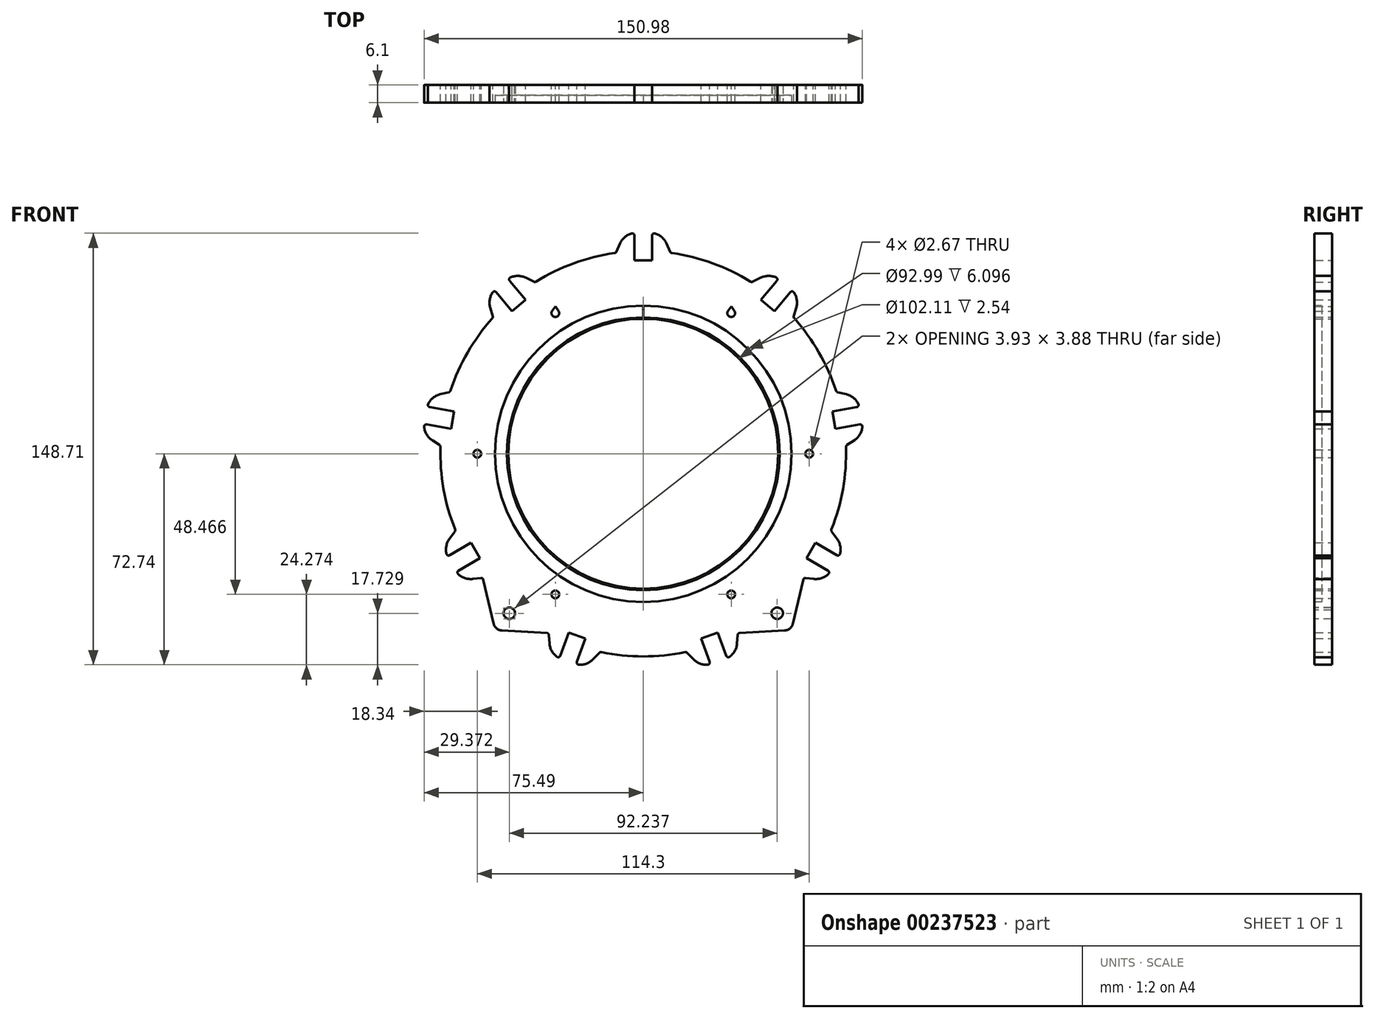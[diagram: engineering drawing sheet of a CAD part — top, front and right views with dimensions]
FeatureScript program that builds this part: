
annotation { "Feature Type Name" : "Feature", "Feature Type Description" : "" }
export const myFeature = defineFeature(function(context is Context, id is Id, definition is map)
    precondition{}
    {
        {
            var Q0;
            Q0=qCreatedBy(makeId("Front.planeOp"),FACE);
            var sketch = newSketch(context, id + "F0", { "sketchPlane" : qUnion([Q0])});
            skCircle(sketch, "E0", {"center": v(0, 0) * mm, "radius": 69.85 * mm});
            skCircle(sketch, "E1", {"center": v(0, 0) * mm, "radius": 46.5 * mm});
            skCircle(sketch, "E2", {"center": v(0, 0) * mm, "radius": 57.15 * mm, "construction": true});
            skPoint(sketch, "E3.center", {"position": v(0, -7.06) * mm});
            skLineSegment(sketch, "E4", {"start": v(-9.44, 69.2) * mm, "end": v(-8.02, 72.42) * mm});
            skLineSegment(sketch, "E5", {"start": v(-2.21, 76.2) * mm, "end": v(2.21, 76.2) * mm});
            skLineSegment(sketch, "E6", {"start": v(8.02, 72.42) * mm, "end": v(9.44, 69.2) * mm});
            skPoint(sketch, "E7", {"position": v(0, 76.2) * mm});
            skLineSegment(sketch, "E8", {"start": v(-3.05, 76.2) * mm, "end": v(-3.05, 66.67) * mm});
            skLineSegment(sketch, "E9", {"start": v(-3.05, 66.67) * mm, "end": v(3.05, 66.67) * mm});
            skLineSegment(sketch, "E10", {"start": v(3.05, 66.67) * mm, "end": v(3.05, 76.2) * mm});
            skPoint(sketch, "E11", {"position": v(0, 66.67) * mm});
            skPoint(sketch, "E12.visualSharp", {"position": v(-6.35, 76.2) * mm});
            skArc(sketch, "E12.filletArc", {"start": v(-2.21, 76.2) * mm, "mid": v(-5.68, 75.17) * mm, "end": v(-8.02, 72.42) * mm});
            skPoint(sketch, "E13.visualSharp", {"position": v(6.35, 76.2) * mm});
            skArc(sketch, "E13.filletArc", {"start": v(8.02, 72.42) * mm, "mid": v(5.68, 75.17) * mm, "end": v(2.21, 76.2) * mm});
            skCircle(sketch, "E14", {"center": v(0, 0) * mm, "radius": 66.72 * mm, "construction": true});
            skLineSegment(sketch, "E15.1.0", {"start": v(-51.72, 46.95) * mm, "end": v(-52.7, 50.32) * mm});
            skArc(sketch, "E15.1.1", {"start": v(-50.68, 56.95) * mm, "mid": v(-52.67, 53.93) * mm, "end": v(-52.7, 50.32) * mm});
            skLineSegment(sketch, "E15.1.2", {"start": v(-51.32, 56.41) * mm, "end": v(-45.2, 49.12) * mm});
            skLineSegment(sketch, "E15.1.3", {"start": v(-40.52, 53.04) * mm, "end": v(-46.65, 60.33) * mm});
            skArc(sketch, "E15.1.4", {"start": v(-40.4, 60.63) * mm, "mid": v(-43.97, 61.23) * mm, "end": v(-47.29, 59.8) * mm});
            skLineSegment(sketch, "E15.1.5", {"start": v(-40.4, 60.63) * mm, "end": v(-37.26, 59.08) * mm});
            skLineSegment(sketch, "E15.1.6", {"start": v(-45.2, 49.12) * mm, "end": v(-40.52, 53.04) * mm});
            skLineSegment(sketch, "E15.2.0", {"start": v(-69.8, 2.72) * mm, "end": v(-72.7, 4.68) * mm});
            skArc(sketch, "E15.2.1", {"start": v(-75.43, 11.05) * mm, "mid": v(-75.01, 7.46) * mm, "end": v(-72.7, 4.68) * mm});
            skLineSegment(sketch, "E15.2.2", {"start": v(-75.57, 10.23) * mm, "end": v(-66.2, 8.58) * mm});
            skLineSegment(sketch, "E15.2.3", {"start": v(-65.13, 14.58) * mm, "end": v(-74.51, 16.23) * mm});
            skArc(sketch, "E15.2.4", {"start": v(-69.92, 20.47) * mm, "mid": v(-73.04, 18.65) * mm, "end": v(-74.66, 15.41) * mm});
            skLineSegment(sketch, "E15.2.5", {"start": v(-69.92, 20.47) * mm, "end": v(-66.52, 21.31) * mm});
            skLineSegment(sketch, "E15.2.6", {"start": v(-66.2, 8.58) * mm, "end": v(-65.13, 14.58) * mm});
            skLineSegment(sketch, "E15.3.0", {"start": v(-55.22, -42.78) * mm, "end": v(-58.7, -43.15) * mm});
            skArc(sketch, "E15.3.1", {"start": v(-64.88, -40.02) * mm, "mid": v(-62.26, -42.5) * mm, "end": v(-58.7, -43.15) * mm});
            skLineSegment(sketch, "E15.3.2", {"start": v(-64.47, -40.74) * mm, "end": v(-56.22, -35.98) * mm});
            skLineSegment(sketch, "E15.3.3", {"start": v(-59.27, -30.7) * mm, "end": v(-67.52, -35.46) * mm});
            skArc(sketch, "E15.3.4", {"start": v(-66.72, -29.26) * mm, "mid": v(-67.94, -32.67) * mm, "end": v(-67.1, -36.18) * mm});
            skLineSegment(sketch, "E15.3.5", {"start": v(-66.72, -29.26) * mm, "end": v(-64.66, -26.43) * mm});
            skLineSegment(sketch, "E15.3.6", {"start": v(-56.22, -35.98) * mm, "end": v(-59.27, -30.7) * mm});
            skLineSegment(sketch, "E15.4.0", {"start": v(-14.8, -68.26) * mm, "end": v(-17.23, -70.8) * mm});
            skArc(sketch, "E15.4.1", {"start": v(-23.98, -72.36) * mm, "mid": v(-20.37, -72.58) * mm, "end": v(-17.23, -70.8) * mm});
            skLineSegment(sketch, "E15.4.2", {"start": v(-23.2, -72.65) * mm, "end": v(-19.94, -63.7) * mm});
            skLineSegment(sketch, "E15.4.3", {"start": v(-25.67, -61.61) * mm, "end": v(-28.93, -70.56) * mm});
            skArc(sketch, "E15.4.4", {"start": v(-32.3, -65.3) * mm, "mid": v(-31.05, -68.7) * mm, "end": v(-28.14, -70.85) * mm});
            skLineSegment(sketch, "E15.4.5", {"start": v(-32.3, -65.3) * mm, "end": v(-32.54, -61.8) * mm});
            skLineSegment(sketch, "E15.4.6", {"start": v(-19.94, -63.7) * mm, "end": v(-25.67, -61.61) * mm});
            skLineSegment(sketch, "E15.5.0", {"start": v(32.54, -61.8) * mm, "end": v(32.3, -65.3) * mm});
            skArc(sketch, "E15.5.1", {"start": v(28.14, -70.85) * mm, "mid": v(31.05, -68.7) * mm, "end": v(32.3, -65.3) * mm});
            skLineSegment(sketch, "E15.5.2", {"start": v(28.93, -70.56) * mm, "end": v(25.67, -61.61) * mm});
            skLineSegment(sketch, "E15.5.3", {"start": v(19.94, -63.7) * mm, "end": v(23.2, -72.65) * mm});
            skArc(sketch, "E15.5.4", {"start": v(17.23, -70.8) * mm, "mid": v(20.37, -72.58) * mm, "end": v(23.98, -72.36) * mm});
            skLineSegment(sketch, "E15.5.5", {"start": v(17.23, -70.8) * mm, "end": v(14.8, -68.26) * mm});
            skLineSegment(sketch, "E15.5.6", {"start": v(25.67, -61.61) * mm, "end": v(19.94, -63.7) * mm});
            skLineSegment(sketch, "E15.6.0", {"start": v(64.66, -26.43) * mm, "end": v(66.72, -29.26) * mm});
            skArc(sketch, "E15.6.1", {"start": v(67.1, -36.18) * mm, "mid": v(67.94, -32.67) * mm, "end": v(66.72, -29.26) * mm});
            skLineSegment(sketch, "E15.6.2", {"start": v(67.52, -35.46) * mm, "end": v(59.27, -30.7) * mm});
            skLineSegment(sketch, "E15.6.3", {"start": v(56.22, -35.98) * mm, "end": v(64.47, -40.74) * mm});
            skArc(sketch, "E15.6.4", {"start": v(58.7, -43.15) * mm, "mid": v(62.26, -42.5) * mm, "end": v(64.88, -40.02) * mm});
            skLineSegment(sketch, "E15.6.5", {"start": v(58.7, -43.15) * mm, "end": v(55.22, -42.78) * mm});
            skLineSegment(sketch, "E15.6.6", {"start": v(59.27, -30.7) * mm, "end": v(56.22, -35.98) * mm});
            skLineSegment(sketch, "E15.7.0", {"start": v(66.52, 21.31) * mm, "end": v(69.92, 20.47) * mm});
            skArc(sketch, "E15.7.1", {"start": v(74.66, 15.41) * mm, "mid": v(73.04, 18.65) * mm, "end": v(69.92, 20.47) * mm});
            skLineSegment(sketch, "E15.7.2", {"start": v(74.51, 16.23) * mm, "end": v(65.13, 14.58) * mm});
            skLineSegment(sketch, "E15.7.3", {"start": v(66.2, 8.58) * mm, "end": v(75.57, 10.23) * mm});
            skArc(sketch, "E15.7.4", {"start": v(72.7, 4.68) * mm, "mid": v(75.01, 7.46) * mm, "end": v(75.43, 11.05) * mm});
            skLineSegment(sketch, "E15.7.5", {"start": v(72.7, 4.68) * mm, "end": v(69.8, 2.72) * mm});
            skLineSegment(sketch, "E15.7.6", {"start": v(65.13, 14.58) * mm, "end": v(66.2, 8.58) * mm});
            skLineSegment(sketch, "E15.8.0", {"start": v(37.26, 59.08) * mm, "end": v(40.4, 60.63) * mm});
            skArc(sketch, "E15.8.1", {"start": v(47.29, 59.8) * mm, "mid": v(43.97, 61.23) * mm, "end": v(40.4, 60.63) * mm});
            skLineSegment(sketch, "E15.8.2", {"start": v(46.65, 60.33) * mm, "end": v(40.52, 53.04) * mm});
            skLineSegment(sketch, "E15.8.3", {"start": v(45.2, 49.12) * mm, "end": v(51.32, 56.41) * mm});
            skArc(sketch, "E15.8.4", {"start": v(52.7, 50.32) * mm, "mid": v(52.67, 53.93) * mm, "end": v(50.68, 56.95) * mm});
            skLineSegment(sketch, "E15.8.5", {"start": v(52.7, 50.32) * mm, "end": v(51.72, 46.95) * mm});
            skLineSegment(sketch, "E15.8.6", {"start": v(40.52, 53.04) * mm, "end": v(45.2, 49.12) * mm});
            skCircle(sketch, "E16", {"center": v(57.15, 0) * mm, "radius": 1.33 * mm});
            skCircle(sketch, "E17", {"center": v(30.28, 48.47) * mm, "radius": 1.33 * mm});
            skCircle(sketch, "E18", {"center": v(30.28, -48.47) * mm, "radius": 1.33 * mm});
            skLineSegment(sketch, "E19", {"start": v(0, 0) * mm, "end": v(30.28, -48.47) * mm, "construction": true});
            skLineSegment(sketch, "E20", {"start": v(30.28, 48.47) * mm, "end": v(0, 0) * mm, "construction": true});
            skCircle(sketch, "E21.MirrorC", {"center": v(-30.28, -48.47) * mm, "radius": 1.33 * mm});
            skCircle(sketch, "E22.MirrorC", {"center": v(-57.15, 0) * mm, "radius": 1.33 * mm});
            skCircle(sketch, "E23.MirrorC", {"center": v(-30.28, 48.47) * mm, "radius": 1.33 * mm});
            skLineSegment(sketch, "E24", {"start": v(31.38, 49.23) * mm, "end": v(30.28, 50.78) * mm});
            skLineSegment(sketch, "E25", {"start": v(30.28, 50.78) * mm, "end": v(29.2, 49.23) * mm});
            skLineSegment(sketch, "E26", {"start": v(-31.38, 49.23) * mm, "end": v(-30.28, 50.78) * mm});
            skLineSegment(sketch, "E27", {"start": v(-30.28, 50.78) * mm, "end": v(-29.2, 49.23) * mm});
            skArc(sketch, "E28", {"start": v(-2.21, 76.2) * mm, "mid": v(-8.62, 74.13) * mm, "end": v(-12.61, 68.7) * mm});
            skArc(sketch, "E29", {"start": v(12.61, 68.7) * mm, "mid": v(9.12, 74.1) * mm, "end": v(3.05, 76.2) * mm});
            skSolve(sketch);
        }
        {
            var Q0;
            Q0=makeQuery(id+"F0.imprint","IMPRINT",FACE,{"disambiguationData":[TD([[makeQuery(id+"F0.imprint","IMPRINT",EDGE,{"derivedFrom":sQuery(id+"F0.wireOp",EDGE,"E1")}),-1.0]])]});
            var Q1;
            {var subQ0=sQuery(id+"F0.wireOp",EDGE,"E15.1.5");Q1=makeQuery(id+"F0.imprint","IMPRINT",FACE,{"disambiguationData":[TD([[makeQuery(id+"F0.imprint","IMPRINT",EDGE,{"derivedFrom":subQ0}),-1.0]])]});}
            var Q2;
            {var subQ0=sQuery(id+"F0.wireOp",EDGE,"E15.1.0");Q2=makeQuery(id+"F0.imprint","IMPRINT",FACE,{"disambiguationData":[TD([[makeQuery(id+"F0.imprint","IMPRINT",EDGE,{"derivedFrom":subQ0}),-1.0]])]});}
            var Q3;
            {var subQ0=sQuery(id+"F0.wireOp",EDGE,"E4");Q3=makeQuery(id+"F0.imprint","IMPRINT",FACE,{"disambiguationData":[TD([[makeQuery(id+"F0.imprint","IMPRINT",EDGE,{"derivedFrom":subQ0}),-1.0]])]});}
            var Q4;
            {var subQ0=sQuery(id+"F0.wireOp",EDGE,"E6");Q4=makeQuery(id+"F0.imprint","IMPRINT",FACE,{"disambiguationData":[TD([[makeQuery(id+"F0.imprint","IMPRINT",EDGE,{"derivedFrom":subQ0}),-1.0]])]});}
            var Q5;
            {var subQ0=sQuery(id+"F0.wireOp",EDGE,"E15.8.0");Q5=makeQuery(id+"F0.imprint","IMPRINT",FACE,{"disambiguationData":[TD([[makeQuery(id+"F0.imprint","IMPRINT",EDGE,{"derivedFrom":subQ0}),-1.0]])]});}
            var Q6;
            {var subQ0=sQuery(id+"F0.wireOp",EDGE,"E15.8.5");Q6=makeQuery(id+"F0.imprint","IMPRINT",FACE,{"disambiguationData":[TD([[makeQuery(id+"F0.imprint","IMPRINT",EDGE,{"derivedFrom":subQ0}),-1.0]])]});}
            var Q7;
            {var subQ0=sQuery(id+"F0.wireOp",EDGE,"E15.7.0");Q7=makeQuery(id+"F0.imprint","IMPRINT",FACE,{"disambiguationData":[TD([[makeQuery(id+"F0.imprint","IMPRINT",EDGE,{"derivedFrom":subQ0}),-1.0]])]});}
            var Q8;
            {var subQ0=sQuery(id+"F0.wireOp",EDGE,"E15.7.5");Q8=makeQuery(id+"F0.imprint","IMPRINT",FACE,{"disambiguationData":[TD([[makeQuery(id+"F0.imprint","IMPRINT",EDGE,{"derivedFrom":subQ0}),-1.0]])]});}
            var Q9;
            {var subQ0=sQuery(id+"F0.wireOp",EDGE,"E15.6.0");Q9=makeQuery(id+"F0.imprint","IMPRINT",FACE,{"disambiguationData":[TD([[makeQuery(id+"F0.imprint","IMPRINT",EDGE,{"derivedFrom":subQ0}),-1.0]])]});}
            var Q10;
            {var subQ0=sQuery(id+"F0.wireOp",EDGE,"E15.6.5");Q10=makeQuery(id+"F0.imprint","IMPRINT",FACE,{"disambiguationData":[TD([[makeQuery(id+"F0.imprint","IMPRINT",EDGE,{"derivedFrom":subQ0}),-1.0]])]});}
            var Q11;
            {var subQ0=sQuery(id+"F0.wireOp",EDGE,"E15.5.5");Q11=makeQuery(id+"F0.imprint","IMPRINT",FACE,{"disambiguationData":[TD([[makeQuery(id+"F0.imprint","IMPRINT",EDGE,{"derivedFrom":subQ0}),-1.0]])]});}
            var Q12;
            {var subQ0=sQuery(id+"F0.wireOp",EDGE,"E15.5.0");Q12=makeQuery(id+"F0.imprint","IMPRINT",FACE,{"disambiguationData":[TD([[makeQuery(id+"F0.imprint","IMPRINT",EDGE,{"derivedFrom":subQ0}),-1.0]])]});}
            var Q13;
            {var subQ0=sQuery(id+"F0.wireOp",EDGE,"E15.4.5");Q13=makeQuery(id+"F0.imprint","IMPRINT",FACE,{"disambiguationData":[TD([[makeQuery(id+"F0.imprint","IMPRINT",EDGE,{"derivedFrom":subQ0}),-1.0]])]});}
            var Q14;
            {var subQ0=sQuery(id+"F0.wireOp",EDGE,"E15.4.0");Q14=makeQuery(id+"F0.imprint","IMPRINT",FACE,{"disambiguationData":[TD([[makeQuery(id+"F0.imprint","IMPRINT",EDGE,{"derivedFrom":subQ0}),-1.0]])]});}
            var Q15;
            {var subQ0=sQuery(id+"F0.wireOp",EDGE,"E15.3.0");Q15=makeQuery(id+"F0.imprint","IMPRINT",FACE,{"disambiguationData":[TD([[makeQuery(id+"F0.imprint","IMPRINT",EDGE,{"derivedFrom":subQ0}),-1.0]])]});}
            var Q16;
            {var subQ0=sQuery(id+"F0.wireOp",EDGE,"E15.3.5");Q16=makeQuery(id+"F0.imprint","IMPRINT",FACE,{"disambiguationData":[TD([[makeQuery(id+"F0.imprint","IMPRINT",EDGE,{"derivedFrom":subQ0}),-1.0]])]});}
            var Q17;
            {var subQ0=sQuery(id+"F0.wireOp",EDGE,"E15.2.0");Q17=makeQuery(id+"F0.imprint","IMPRINT",FACE,{"disambiguationData":[TD([[makeQuery(id+"F0.imprint","IMPRINT",EDGE,{"derivedFrom":subQ0}),-1.0]])]});}
            var Q18;
            {var subQ0=sQuery(id+"F0.wireOp",EDGE,"E15.2.5");Q18=makeQuery(id+"F0.imprint","IMPRINT",FACE,{"disambiguationData":[TD([[makeQuery(id+"F0.imprint","IMPRINT",EDGE,{"derivedFrom":subQ0}),-1.0]])]});}
            extrude(context, id + "F1", {"entities" : qUnion([Q0, Q1, Q2, Q3, Q4, Q5, Q6, Q7, Q8, Q9, Q10, Q11, Q12, Q13, Q14, Q15, Q16, Q17, Q18]), "offsetDistance" : 25.4 * mm, "depth" : 6.1 * mm});
        }
        {
            var Q0;
            Q0=makeQuery(id+"F1.opExtrude","CAP_FACE",FACE,{"disambiguationData":[OSD([sQuery(id+"F0.wireOp",EDGE,"E0"),sQuery(id+"F0.wireOp",EDGE,"E1"),sQuery(id+"F0.wireOp",EDGE,"s7rXqqL2-3z2l-88EV-UIsY-hwb08Po9ZJjJ"),sQuery(id+"F0.wireOp",EDGE,"E3.1.0"),sQuery(id+"F0.wireOp",EDGE,"E3.2.0"),sQuery(id+"F0.wireOp",EDGE,"E3.3.0"),sQuery(id+"F0.wireOp",EDGE,"E4"),sQuery(id+"F0.wireOp",EDGE,"E6"),sQuery(id+"F0.wireOp",EDGE,"E8"),sQuery(id+"F0.wireOp",EDGE,"E9"),sQuery(id+"F0.wireOp",EDGE,"E10"),sQuery(id+"F0.wireOp",EDGE,"E12.filletArc"),sQuery(id+"F0.wireOp",EDGE,"E13.filletArc"),sQuery(id+"F0.wireOp",EDGE,"e3144966-756d-47fd-8283-5f46bd2110e0.1.0"),sQuery(id+"F0.wireOp",EDGE,"e3144966-756d-47fd-8283-5f46bd2110e0.1.1"),sQuery(id+"F0.wireOp",EDGE,"e3144966-756d-47fd-8283-5f46bd2110e0.1.2"),sQuery(id+"F0.wireOp",EDGE,"e3144966-756d-47fd-8283-5f46bd2110e0.1.3"),sQuery(id+"F0.wireOp",EDGE,"e3144966-756d-47fd-8283-5f46bd2110e0.1.4"),sQuery(id+"F0.wireOp",EDGE,"e3144966-756d-47fd-8283-5f46bd2110e0.1.6"),sQuery(id+"F0.wireOp",EDGE,"e3144966-756d-47fd-8283-5f46bd2110e0.1.7"),sQuery(id+"F0.wireOp",EDGE,"e3144966-756d-47fd-8283-5f46bd2110e0.2.0"),sQuery(id+"F0.wireOp",EDGE,"e3144966-756d-47fd-8283-5f46bd2110e0.2.1"),sQuery(id+"F0.wireOp",EDGE,"e3144966-756d-47fd-8283-5f46bd2110e0.2.2"),sQuery(id+"F0.wireOp",EDGE,"e3144966-756d-47fd-8283-5f46bd2110e0.2.3"),sQuery(id+"F0.wireOp",EDGE,"e3144966-756d-47fd-8283-5f46bd2110e0.2.4"),sQuery(id+"F0.wireOp",EDGE,"e3144966-756d-47fd-8283-5f46bd2110e0.2.6"),sQuery(id+"F0.wireOp",EDGE,"e3144966-756d-47fd-8283-5f46bd2110e0.2.7"),sQuery(id+"F0.wireOp",EDGE,"e3144966-756d-47fd-8283-5f46bd2110e0.3.0"),sQuery(id+"F0.wireOp",EDGE,"e3144966-756d-47fd-8283-5f46bd2110e0.3.1"),sQuery(id+"F0.wireOp",EDGE,"e3144966-756d-47fd-8283-5f46bd2110e0.3.2"),sQuery(id+"F0.wireOp",EDGE,"e3144966-756d-47fd-8283-5f46bd2110e0.3.3"),sQuery(id+"F0.wireOp",EDGE,"e3144966-756d-47fd-8283-5f46bd2110e0.3.4"),sQuery(id+"F0.wireOp",EDGE,"e3144966-756d-47fd-8283-5f46bd2110e0.3.6"),sQuery(id+"F0.wireOp",EDGE,"e3144966-756d-47fd-8283-5f46bd2110e0.3.7"),sQuery(id+"F0.wireOp",EDGE,"e3144966-756d-47fd-8283-5f46bd2110e0.4.0"),sQuery(id+"F0.wireOp",EDGE,"e3144966-756d-47fd-8283-5f46bd2110e0.4.1"),sQuery(id+"F0.wireOp",EDGE,"e3144966-756d-47fd-8283-5f46bd2110e0.4.2"),sQuery(id+"F0.wireOp",EDGE,"e3144966-756d-47fd-8283-5f46bd2110e0.4.3"),sQuery(id+"F0.wireOp",EDGE,"e3144966-756d-47fd-8283-5f46bd2110e0.4.4"),sQuery(id+"F0.wireOp",EDGE,"e3144966-756d-47fd-8283-5f46bd2110e0.4.6"),sQuery(id+"F0.wireOp",EDGE,"e3144966-756d-47fd-8283-5f46bd2110e0.4.7"),sQuery(id+"F0.wireOp",EDGE,"e3144966-756d-47fd-8283-5f46bd2110e0.5.0"),sQuery(id+"F0.wireOp",EDGE,"e3144966-756d-47fd-8283-5f46bd2110e0.5.1"),sQuery(id+"F0.wireOp",EDGE,"e3144966-756d-47fd-8283-5f46bd2110e0.5.2"),sQuery(id+"F0.wireOp",EDGE,"e3144966-756d-47fd-8283-5f46bd2110e0.5.3"),sQuery(id+"F0.wireOp",EDGE,"e3144966-756d-47fd-8283-5f46bd2110e0.5.4"),sQuery(id+"F0.wireOp",EDGE,"e3144966-756d-47fd-8283-5f46bd2110e0.5.6"),sQuery(id+"F0.wireOp",EDGE,"e3144966-756d-47fd-8283-5f46bd2110e0.5.7"),sQuery(id+"F0.wireOp",EDGE,"e3144966-756d-47fd-8283-5f46bd2110e0.6.0"),sQuery(id+"F0.wireOp",EDGE,"e3144966-756d-47fd-8283-5f46bd2110e0.6.1"),sQuery(id+"F0.wireOp",EDGE,"e3144966-756d-47fd-8283-5f46bd2110e0.6.2"),sQuery(id+"F0.wireOp",EDGE,"e3144966-756d-47fd-8283-5f46bd2110e0.6.3"),sQuery(id+"F0.wireOp",EDGE,"e3144966-756d-47fd-8283-5f46bd2110e0.6.4"),sQuery(id+"F0.wireOp",EDGE,"e3144966-756d-47fd-8283-5f46bd2110e0.6.6"),sQuery(id+"F0.wireOp",EDGE,"e3144966-756d-47fd-8283-5f46bd2110e0.6.7"),sQuery(id+"F0.wireOp",EDGE,"e3144966-756d-47fd-8283-5f46bd2110e0.7.0"),sQuery(id+"F0.wireOp",EDGE,"e3144966-756d-47fd-8283-5f46bd2110e0.7.1"),sQuery(id+"F0.wireOp",EDGE,"e3144966-756d-47fd-8283-5f46bd2110e0.7.2"),sQuery(id+"F0.wireOp",EDGE,"e3144966-756d-47fd-8283-5f46bd2110e0.7.3"),sQuery(id+"F0.wireOp",EDGE,"e3144966-756d-47fd-8283-5f46bd2110e0.7.4"),sQuery(id+"F0.wireOp",EDGE,"e3144966-756d-47fd-8283-5f46bd2110e0.7.6"),sQuery(id+"F0.wireOp",EDGE,"e3144966-756d-47fd-8283-5f46bd2110e0.7.7"),sQuery(id+"F0.wireOp",EDGE,"e3144966-756d-47fd-8283-5f46bd2110e0.8.0"),sQuery(id+"F0.wireOp",EDGE,"e3144966-756d-47fd-8283-5f46bd2110e0.8.1"),sQuery(id+"F0.wireOp",EDGE,"e3144966-756d-47fd-8283-5f46bd2110e0.8.2"),sQuery(id+"F0.wireOp",EDGE,"e3144966-756d-47fd-8283-5f46bd2110e0.8.3"),sQuery(id+"F0.wireOp",EDGE,"e3144966-756d-47fd-8283-5f46bd2110e0.8.4"),sQuery(id+"F0.wireOp",EDGE,"e3144966-756d-47fd-8283-5f46bd2110e0.8.6"),sQuery(id+"F0.wireOp",EDGE,"e3144966-756d-47fd-8283-5f46bd2110e0.8.7")])],"isStart":false});
            var sketch = newSketch(context, id + "F2", { "sketchPlane" : qUnion([Q0])});
            skCircle(sketch, "E30", {"center": v(0, 0) * mm, "radius": 47 * mm});
            skCircle(sketch, "E31", {"center": v(0, 0) * mm, "radius": 51.05 * mm});
            skSolve(sketch);
        }
        {
            var Q0;
            Q0=makeQuery(id+"F2.imprint","IMPRINT",FACE,{"disambiguationData":[TD([[makeQuery(id+"F2.imprint","IMPRINT",EDGE,{"derivedFrom":sQuery(id+"F2.wireOp",EDGE,"E31")}),1.0]])]});
            extrude(context, id + "F3", {"entities" : qUnion([Q0]), "operationType" : NewBodyOperationType.REMOVE, "oppositeDirection" : true, "depth" : 2.54 * mm});
        }
        {
            var Q0;
            {var subQ0=sQuery(id+"F0.wireOp",EDGE,"E15.5.2");var subQ1=sQuery(id+"F0.wireOp",EDGE,"E15.5.0");var subQ2=sQuery(id+"F0.wireOp",EDGE,"E15.5.5");var subQ3=sQuery(id+"F0.wireOp",EDGE,"E15.4.5");var subQ4=sQuery(id+"F0.wireOp",EDGE,"E15.4.6");var subQ5=sQuery(id+"F0.wireOp",EDGE,"E15.4.4");var subQ6=sQuery(id+"F0.wireOp",EDGE,"E15.5.3");var subQ7=sQuery(id+"F0.wireOp",EDGE,"E15.4.2");var subQ8=sQuery(id+"F0.wireOp",EDGE,"E15.4.0");var subQ9=sQuery(id+"F0.wireOp",EDGE,"E15.3.5");var subQ10=sQuery(id+"F0.wireOp",EDGE,"E15.3.3");var subQ11=sQuery(id+"F0.wireOp",EDGE,"E15.2.5");var subQ12=sQuery(id+"F0.wireOp",EDGE,"E15.3.1");var subQ13=sQuery(id+"F0.wireOp",EDGE,"E29");var subQ14=sQuery(id+"F0.wireOp",EDGE,"E15.5.4");var subQ15=sQuery(id+"F0.wireOp",EDGE,"E15.4.3");var subQ16=sQuery(id+"F0.wireOp",EDGE,"E15.4.1");var subQ17=sQuery(id+"F0.wireOp",EDGE,"E15.3.0");var subQ18=sQuery(id+"F0.wireOp",EDGE,"E28");var subQ19=sQuery(id+"F0.wireOp",EDGE,"E15.2.6");var subQ20=sQuery(id+"F0.wireOp",EDGE,"E27");var subQ21=sQuery(id+"F0.wireOp",EDGE,"E15.2.4");var subQ22=sQuery(id+"F0.wireOp",EDGE,"E25");var subQ23=sQuery(id+"F0.wireOp",EDGE,"E15.3.6");var subQ24=sQuery(id+"F0.wireOp",EDGE,"E15.3.4");var subQ25=sQuery(id+"F0.wireOp",EDGE,"E15.2.3");var subQ26=sQuery(id+"F0.wireOp",EDGE,"E0");var subQ27=sQuery(id+"F0.wireOp",EDGE,"E15.6.5");var subQ28=sQuery(id+"F0.wireOp",EDGE,"E15.7.4");var subQ29=sQuery(id+"F0.wireOp",EDGE,"E15.1.1");var subQ30=sQuery(id+"F0.wireOp",EDGE,"E17");var subQ31=sQuery(id+"F0.wireOp",EDGE,"E15.2.0");var subQ32=sQuery(id+"F0.wireOp",EDGE,"E15.2.2");var subQ33=sQuery(id+"F0.wireOp",EDGE,"E23.MirrorC");var subQ34=sQuery(id+"F0.wireOp",EDGE,"E15.7.0");var subQ35=sQuery(id+"F0.wireOp",EDGE,"E15.8.5");var subQ36=sQuery(id+"F0.wireOp",EDGE,"E15.8.0");var subQ37=sQuery(id+"F0.wireOp",EDGE,"E15.8.4");var subQ38=sQuery(id+"F0.wireOp",EDGE,"E15.1.5");var subQ39=sQuery(id+"F0.wireOp",EDGE,"E15.5.1");var subQ40=sQuery(id+"F0.wireOp",EDGE,"E15.1.0");var subQ41=sQuery(id+"F0.wireOp",EDGE,"E9");var subQ42=sQuery(id+"F0.wireOp",EDGE,"E15.8.1");var subQ43=sQuery(id+"F0.wireOp",EDGE,"E15.1.2");var subQ44=sQuery(id+"F0.wireOp",EDGE,"E15.7.3");var subQ45=sQuery(id+"F0.wireOp",EDGE,"E15.1.4");var subQ46=sQuery(id+"F0.wireOp",EDGE,"E8");var subQ47=sQuery(id+"F0.wireOp",EDGE,"E15.3.2");var subQ48=sQuery(id+"F0.wireOp",EDGE,"E15.2.1");var subQ49=sQuery(id+"F0.wireOp",EDGE,"E15.1.6");var subQ50=sQuery(id+"F0.wireOp",EDGE,"E15.8.3");var subQ51=sQuery(id+"F0.wireOp",EDGE,"E10");var subQ52=sQuery(id+"F0.wireOp",EDGE,"E15.8.2");var subQ53=sQuery(id+"F0.wireOp",EDGE,"E15.6.0");var subQ54=sQuery(id+"F0.wireOp",EDGE,"E15.7.5");var subQ55=sQuery(id+"F0.wireOp",EDGE,"E15.1.3");var subQ56=sQuery(id+"F0.wireOp",EDGE,"E15.5.6");var subQ57=sQuery(id+"F0.wireOp",EDGE,"E26");var subQ58=sQuery(id+"F0.wireOp",EDGE,"E15.6.1");var subQ59=sQuery(id+"F0.wireOp",EDGE,"E15.6.2");var subQ60=sQuery(id+"F0.wireOp",EDGE,"E15.6.3");var subQ61=sQuery(id+"F0.wireOp",EDGE,"E15.6.4");var subQ62=sQuery(id+"F0.wireOp",EDGE,"E24");var subQ63=sQuery(id+"F0.wireOp",EDGE,"E15.6.6");var subQ64=sQuery(id+"F0.wireOp",EDGE,"E15.7.1");var subQ65=sQuery(id+"F0.wireOp",EDGE,"E15.7.2");var subQ66=sQuery(id+"F0.wireOp",EDGE,"E15.7.6");var subQ67=sQuery(id+"F0.wireOp",EDGE,"E15.8.6");var subQ68=sQuery(id+"F0.wireOp",EDGE,"E16");var subQ69=sQuery(id+"F0.wireOp",EDGE,"E18");var subQ70=sQuery(id+"F0.wireOp",EDGE,"E21.MirrorC");var subQ71=sQuery(id+"F0.wireOp",EDGE,"E22.MirrorC");Q0=makeQuery(id+"F3.boolean.opBoolean","SPLIT",FACE,{"disambiguationData":[TD([makeQuery(id+"F1.opExtrude","SWEPT_FACE",FACE,{"disambiguationData":[OSD([subQ46])]})])],"derivedFrom":makeQuery(id+"F1.opExtrude","CAP_FACE",FACE,{"disambiguationData":[OSD([subQ26,sQuery(id+"F0.wireOp",EDGE,"E1"),subQ46,subQ41,subQ51,subQ40,subQ29,subQ43,subQ55,subQ45,subQ38,subQ49,subQ31,subQ48,subQ32,subQ25,subQ21,subQ11,subQ19,subQ17,subQ12,subQ47,subQ10,subQ24,subQ9,subQ23,subQ8,subQ16,subQ7,subQ15,subQ5,subQ3,subQ4,subQ1,subQ39,subQ0,subQ6,subQ14,subQ2,subQ56,subQ53,subQ58,subQ59,subQ60,subQ61,subQ27,subQ63,subQ34,subQ64,subQ65,subQ44,subQ28,subQ54,subQ66,subQ36,subQ42,subQ52,subQ50,subQ37,subQ35,subQ67,subQ68,subQ30,subQ69,subQ70,subQ71,subQ33,subQ62,subQ22,subQ57,subQ20,subQ18,subQ13])],"isStart":false})});}
            var sketch = newSketch(context, id + "F4", { "sketchPlane" : qUnion([Q0])});
            skLineSegment(sketch, "E32", {"start": v(-0.03, 51.05) * mm, "end": v(-0.03, 46.99) * mm});
            skLineSegment(sketch, "E33", {"start": v(0.03, 46.99) * mm, "end": v(0.03, 51.05) * mm});
            skArc(sketch, "E34", {"start": v(0.03, 46.99) * mm, "mid": v(0, 46.99) * mm, "end": v(-0.03, 46.99) * mm});
            skArc(sketch, "E35", {"start": v(0.03, 51.05) * mm, "mid": v(0, 51.05) * mm, "end": v(-0.03, 51.05) * mm});
            skPoint(sketch, "E36.positionSnap0", {"position": v(0, 47) * mm});
            skSolve(sketch);
        }
        {
            var Q0;
            Q0=qSketchRegion(id+"F4",true);
            var Q1;
            Q1=makeQuery(id+"F3.boolean.opBoolean","COPY",FACE,{"derivedFrom":makeQuery(id+"F3.opExtrude","CAP_FACE",FACE,{"disambiguationData":[OSD([sQuery(id+"F2.wireOp",EDGE,"E30"),sQuery(id+"F2.wireOp",EDGE,"E31")])],"isStart":false})});
            extrude(context, id + "F5", {"entities" : qUnion([Q0]), "operationType" : NewBodyOperationType.ADD, "endBound" : BoundingType.UP_TO_SURFACE, "oppositeDirection" : true, "endBoundEntityFace" : qUnion([Q1]), "depth" : 25.4 * mm});
        }
        {
            var Q0;
            {var subQ0=sQuery(id+"F4.wireOp",EDGE,"E35");var subQ1=sQuery(id+"F4.wireOp",EDGE,"E34");var subQ2=sQuery(id+"F4.wireOp",EDGE,"E33");var subQ3=sQuery(id+"F4.wireOp",EDGE,"E32");var subQ4=sQuery(id+"F0.wireOp",EDGE,"E1");var subQ5=sQuery(id+"F0.wireOp",EDGE,"E27");var subQ6=sQuery(id+"F0.wireOp",EDGE,"E26");var subQ7=sQuery(id+"F0.wireOp",EDGE,"E25");var subQ8=sQuery(id+"F0.wireOp",EDGE,"E24");var subQ9=sQuery(id+"F0.wireOp",EDGE,"E23.MirrorC");var subQ10=sQuery(id+"F0.wireOp",EDGE,"E22.MirrorC");var subQ11=sQuery(id+"F0.wireOp",EDGE,"E21.MirrorC");var subQ12=sQuery(id+"F0.wireOp",EDGE,"E18");var subQ13=sQuery(id+"F0.wireOp",EDGE,"E17");var subQ14=sQuery(id+"F0.wireOp",EDGE,"E16");var subQ15=sQuery(id+"F0.wireOp",EDGE,"E15.8.6");var subQ16=sQuery(id+"F0.wireOp",EDGE,"E15.8.5");var subQ17=sQuery(id+"F0.wireOp",EDGE,"E15.8.4");var subQ18=sQuery(id+"F0.wireOp",EDGE,"E15.8.3");var subQ19=sQuery(id+"F0.wireOp",EDGE,"E15.8.2");var subQ20=sQuery(id+"F0.wireOp",EDGE,"E15.8.1");var subQ21=sQuery(id+"F0.wireOp",EDGE,"E15.8.0");var subQ22=sQuery(id+"F0.wireOp",EDGE,"E15.7.6");var subQ23=sQuery(id+"F0.wireOp",EDGE,"E15.7.5");var subQ24=sQuery(id+"F0.wireOp",EDGE,"E15.7.4");var subQ25=sQuery(id+"F0.wireOp",EDGE,"E15.7.3");var subQ26=sQuery(id+"F0.wireOp",EDGE,"E15.7.2");var subQ27=sQuery(id+"F0.wireOp",EDGE,"E15.7.1");var subQ28=sQuery(id+"F0.wireOp",EDGE,"E15.7.0");var subQ29=sQuery(id+"F0.wireOp",EDGE,"E15.6.6");var subQ30=sQuery(id+"F0.wireOp",EDGE,"E15.6.5");var subQ31=sQuery(id+"F0.wireOp",EDGE,"E15.6.4");var subQ32=sQuery(id+"F0.wireOp",EDGE,"E15.6.3");var subQ33=sQuery(id+"F0.wireOp",EDGE,"E15.6.2");var subQ34=sQuery(id+"F0.wireOp",EDGE,"E15.6.1");var subQ35=sQuery(id+"F0.wireOp",EDGE,"E15.6.0");var subQ36=sQuery(id+"F0.wireOp",EDGE,"E15.5.6");var subQ37=sQuery(id+"F0.wireOp",EDGE,"E15.5.5");var subQ38=sQuery(id+"F0.wireOp",EDGE,"E15.5.4");var subQ39=sQuery(id+"F0.wireOp",EDGE,"E15.5.3");var subQ40=sQuery(id+"F0.wireOp",EDGE,"E15.5.2");var subQ41=sQuery(id+"F0.wireOp",EDGE,"E15.5.1");var subQ42=sQuery(id+"F0.wireOp",EDGE,"E15.5.0");var subQ43=sQuery(id+"F0.wireOp",EDGE,"E15.4.6");var subQ44=sQuery(id+"F0.wireOp",EDGE,"E15.4.5");var subQ45=sQuery(id+"F0.wireOp",EDGE,"E15.4.4");var subQ46=sQuery(id+"F0.wireOp",EDGE,"E15.4.3");var subQ47=sQuery(id+"F0.wireOp",EDGE,"E15.4.2");var subQ48=sQuery(id+"F0.wireOp",EDGE,"E15.4.1");var subQ49=sQuery(id+"F0.wireOp",EDGE,"E15.4.0");var subQ50=sQuery(id+"F0.wireOp",EDGE,"E15.3.6");var subQ51=sQuery(id+"F0.wireOp",EDGE,"E15.3.5");var subQ52=sQuery(id+"F0.wireOp",EDGE,"E15.3.4");var subQ53=sQuery(id+"F0.wireOp",EDGE,"E15.3.3");var subQ54=sQuery(id+"F0.wireOp",EDGE,"E15.3.2");var subQ55=sQuery(id+"F0.wireOp",EDGE,"E15.3.1");var subQ56=sQuery(id+"F0.wireOp",EDGE,"E15.3.0");var subQ57=sQuery(id+"F0.wireOp",EDGE,"E15.2.6");var subQ58=sQuery(id+"F0.wireOp",EDGE,"E15.2.5");var subQ59=sQuery(id+"F0.wireOp",EDGE,"E15.2.4");var subQ60=sQuery(id+"F0.wireOp",EDGE,"E15.2.3");var subQ61=sQuery(id+"F0.wireOp",EDGE,"E15.2.2");var subQ62=sQuery(id+"F0.wireOp",EDGE,"E15.2.1");var subQ63=sQuery(id+"F0.wireOp",EDGE,"E15.2.0");var subQ64=sQuery(id+"F0.wireOp",EDGE,"E15.1.6");var subQ65=sQuery(id+"F0.wireOp",EDGE,"E15.1.5");var subQ66=sQuery(id+"F0.wireOp",EDGE,"E15.1.4");var subQ67=sQuery(id+"F0.wireOp",EDGE,"E15.1.3");var subQ68=sQuery(id+"F0.wireOp",EDGE,"E15.1.2");var subQ69=sQuery(id+"F0.wireOp",EDGE,"E15.1.1");var subQ70=sQuery(id+"F0.wireOp",EDGE,"E15.1.0");var subQ71=sQuery(id+"F0.wireOp",EDGE,"E13.filletArc");var subQ72=sQuery(id+"F0.wireOp",EDGE,"E12.filletArc");var subQ73=sQuery(id+"F0.wireOp",EDGE,"E10");var subQ74=sQuery(id+"F0.wireOp",EDGE,"E9");var subQ75=sQuery(id+"F0.wireOp",EDGE,"E8");var subQ76=sQuery(id+"F0.wireOp",EDGE,"E6");var subQ77=sQuery(id+"F0.wireOp",EDGE,"E4");var subQ78=sQuery(id+"F0.wireOp",EDGE,"E0");var subQ79=makeQuery(id+"F1.opExtrude","CAP_FACE",FACE,{"disambiguationData":[OSD([subQ78,subQ4,subQ77,subQ76,subQ75,subQ74,subQ73,subQ72,subQ71,subQ70,subQ69,subQ68,subQ67,subQ66,subQ65,subQ64,subQ63,subQ62,subQ61,subQ60,subQ59,subQ58,subQ57,subQ56,subQ55,subQ54,subQ53,subQ52,subQ51,subQ50,subQ49,subQ48,subQ47,subQ46,subQ45,subQ44,subQ43,subQ42,subQ41,subQ40,subQ39,subQ38,subQ37,subQ36,subQ35,subQ34,subQ33,subQ32,subQ31,subQ30,subQ29,subQ28,subQ27,subQ26,subQ25,subQ24,subQ23,subQ22,subQ21,subQ20,subQ19,subQ18,subQ17,subQ16,subQ15,subQ14,subQ13,subQ12,subQ11,subQ10,subQ9,subQ8,subQ7,subQ6,subQ5])],"isStart":false});Q0=makeQuery(id+"F3rWmamWYXU4C0m_1.1.F5.boolean.opBoolean","MERGE",FACE,{"derivedFrom":[makeQuery(id+"F5.boolean.opBoolean","MERGE",FACE,{"derivedFrom":[makeQuery(id+"F3.boolean.opBoolean","SPLIT",FACE,{"disambiguationData":[TD([makeQuery(id+"F1.opExtrude","SWEPT_FACE",FACE,{"disambiguationData":[OSD([subQ77])]})])],"derivedFrom":subQ79}),makeQuery(id+"F3.boolean.opBoolean","SPLIT",FACE,{"disambiguationData":[TD([makeQuery(id+"F1.opExtrude","SWEPT_FACE",FACE,{"disambiguationData":[OSD([subQ4])]})])],"derivedFrom":subQ79}),makeQuery(id+"F5.opExtrude","CAP_FACE",FACE,{"disambiguationData":[OSD([subQ3,subQ2,subQ1,subQ0])],"isStart":true})]}),makeQuery(id+"F3rWmamWYXU4C0m_1.1.F5.opExtrude","CAP_FACE",FACE,{"disambiguationData":[OSD([subQ3,subQ2,subQ1,subQ0])],"isStart":true})]});}
            var sketch = newSketch(context, id + "F6", { "sketchPlane" : qUnion([Q0])});
            skLineSegment(sketch, "E37", {"start": v(-55.22, -42.78) * mm, "end": v(-51.56, -58.48) * mm});
            skLineSegment(sketch, "E38", {"start": v(-48.64, -60.93) * mm, "end": v(-32.54, -61.8) * mm});
            skLineSegment(sketch, "E39", {"start": v(32.54, -61.8) * mm, "end": v(48.64, -60.93) * mm});
            skLineSegment(sketch, "E40", {"start": v(51.56, -58.48) * mm, "end": v(55.22, -42.78) * mm});
            skLineSegment(sketch, "E41", {"start": v(-44.9, -53.5) * mm, "end": v(-51.02, -60.8) * mm, "construction": true});
            skLineSegment(sketch, "E42", {"start": v(44.9, -53.5) * mm, "end": v(51.02, -60.8) * mm, "construction": true});
            skCircle(sketch, "E43", {"center": v(-46.12, -54.97) * mm, "radius": 1.98 * mm});
            skCircle(sketch, "E44", {"center": v(46.12, -54.97) * mm, "radius": 1.98 * mm});
            skPoint(sketch, "E45.visualSharp", {"position": v(-51.02, -60.8) * mm});
            skArc(sketch, "E45.filletArc", {"start": v(-51.56, -58.48) * mm, "mid": v(-50.51, -60.2) * mm, "end": v(-48.64, -60.93) * mm});
            skPoint(sketch, "E46.visualSharp", {"position": v(51.02, -60.8) * mm});
            skArc(sketch, "E46.filletArc", {"start": v(48.64, -60.93) * mm, "mid": v(50.51, -60.2) * mm, "end": v(51.56, -58.48) * mm});
            skSolve(sketch);
        }
        {
            var Q0;
            Q0=makeQuery(id+"F6.imprint","IMPRINT",FACE,{"disambiguationData":[TD([[makeQuery(id+"F6.imprint","IMPRINT",EDGE,{"derivedFrom":sQuery(id+"F6.wireOp",EDGE,"E37")}),1.0]])]});
            var Q1;
            Q1=makeQuery(id+"F6.imprint","IMPRINT",FACE,{"disambiguationData":[TD([[makeQuery(id+"F6.imprint","IMPRINT",EDGE,{"derivedFrom":sQuery(id+"F6.wireOp",EDGE,"E39")}),1.0]])]});
            var Q2;
            Q2=makeQuery(id+"F1.opExtrude","CAP_FACE",FACE,{"disambiguationData":[OSD([sQuery(id+"F0.wireOp",EDGE,"E0"),sQuery(id+"F0.wireOp",EDGE,"E1"),sQuery(id+"F0.wireOp",EDGE,"E4"),sQuery(id+"F0.wireOp",EDGE,"E6"),sQuery(id+"F0.wireOp",EDGE,"E8"),sQuery(id+"F0.wireOp",EDGE,"E9"),sQuery(id+"F0.wireOp",EDGE,"E10"),sQuery(id+"F0.wireOp",EDGE,"E12.filletArc"),sQuery(id+"F0.wireOp",EDGE,"E13.filletArc"),sQuery(id+"F0.wireOp",EDGE,"E15.1.0"),sQuery(id+"F0.wireOp",EDGE,"E15.1.1"),sQuery(id+"F0.wireOp",EDGE,"E15.1.2"),sQuery(id+"F0.wireOp",EDGE,"E15.1.3"),sQuery(id+"F0.wireOp",EDGE,"E15.1.4"),sQuery(id+"F0.wireOp",EDGE,"E15.1.5"),sQuery(id+"F0.wireOp",EDGE,"E15.1.6"),sQuery(id+"F0.wireOp",EDGE,"E15.2.0"),sQuery(id+"F0.wireOp",EDGE,"E15.2.1"),sQuery(id+"F0.wireOp",EDGE,"E15.2.2"),sQuery(id+"F0.wireOp",EDGE,"E15.2.3"),sQuery(id+"F0.wireOp",EDGE,"E15.2.4"),sQuery(id+"F0.wireOp",EDGE,"E15.2.5"),sQuery(id+"F0.wireOp",EDGE,"E15.2.6"),sQuery(id+"F0.wireOp",EDGE,"E15.3.0"),sQuery(id+"F0.wireOp",EDGE,"E15.3.1"),sQuery(id+"F0.wireOp",EDGE,"E15.3.2"),sQuery(id+"F0.wireOp",EDGE,"E15.3.3"),sQuery(id+"F0.wireOp",EDGE,"E15.3.4"),sQuery(id+"F0.wireOp",EDGE,"E15.3.5"),sQuery(id+"F0.wireOp",EDGE,"E15.3.6"),sQuery(id+"F0.wireOp",EDGE,"E15.4.0"),sQuery(id+"F0.wireOp",EDGE,"E15.4.1"),sQuery(id+"F0.wireOp",EDGE,"E15.4.2"),sQuery(id+"F0.wireOp",EDGE,"E15.4.3"),sQuery(id+"F0.wireOp",EDGE,"E15.4.4"),sQuery(id+"F0.wireOp",EDGE,"E15.4.5"),sQuery(id+"F0.wireOp",EDGE,"E15.4.6"),sQuery(id+"F0.wireOp",EDGE,"E15.5.0"),sQuery(id+"F0.wireOp",EDGE,"E15.5.1"),sQuery(id+"F0.wireOp",EDGE,"E15.5.2"),sQuery(id+"F0.wireOp",EDGE,"E15.5.3"),sQuery(id+"F0.wireOp",EDGE,"E15.5.4"),sQuery(id+"F0.wireOp",EDGE,"E15.5.5"),sQuery(id+"F0.wireOp",EDGE,"E15.5.6"),sQuery(id+"F0.wireOp",EDGE,"E15.6.0"),sQuery(id+"F0.wireOp",EDGE,"E15.6.1"),sQuery(id+"F0.wireOp",EDGE,"E15.6.2"),sQuery(id+"F0.wireOp",EDGE,"E15.6.3"),sQuery(id+"F0.wireOp",EDGE,"E15.6.4"),sQuery(id+"F0.wireOp",EDGE,"E15.6.5"),sQuery(id+"F0.wireOp",EDGE,"E15.6.6"),sQuery(id+"F0.wireOp",EDGE,"E15.7.0"),sQuery(id+"F0.wireOp",EDGE,"E15.7.1"),sQuery(id+"F0.wireOp",EDGE,"E15.7.2"),sQuery(id+"F0.wireOp",EDGE,"E15.7.3"),sQuery(id+"F0.wireOp",EDGE,"E15.7.4"),sQuery(id+"F0.wireOp",EDGE,"E15.7.5"),sQuery(id+"F0.wireOp",EDGE,"E15.7.6"),sQuery(id+"F0.wireOp",EDGE,"E15.8.0"),sQuery(id+"F0.wireOp",EDGE,"E15.8.1"),sQuery(id+"F0.wireOp",EDGE,"E15.8.2"),sQuery(id+"F0.wireOp",EDGE,"E15.8.3"),sQuery(id+"F0.wireOp",EDGE,"E15.8.4"),sQuery(id+"F0.wireOp",EDGE,"E15.8.5"),sQuery(id+"F0.wireOp",EDGE,"E15.8.6"),sQuery(id+"F0.wireOp",EDGE,"E16"),sQuery(id+"F0.wireOp",EDGE,"E17"),sQuery(id+"F0.wireOp",EDGE,"E18"),sQuery(id+"F0.wireOp",EDGE,"E21.MirrorC"),sQuery(id+"F0.wireOp",EDGE,"E22.MirrorC"),sQuery(id+"F0.wireOp",EDGE,"E23.MirrorC"),sQuery(id+"F0.wireOp",EDGE,"E24"),sQuery(id+"F0.wireOp",EDGE,"E25"),sQuery(id+"F0.wireOp",EDGE,"E26"),sQuery(id+"F0.wireOp",EDGE,"E27")])],"isStart":true});
            extrude(context, id + "F7", {"entities" : qUnion([Q0, Q1]), "operationType" : NewBodyOperationType.ADD, "endBound" : BoundingType.UP_TO_SURFACE, "oppositeDirection" : true, "endBoundEntityFace" : qUnion([Q2]), "depth" : 25.4 * mm});
        }
        {
            var Q0;
            Q0=makeQuery(id+"F1.opExtrude","SWEPT_EDGE",EDGE,{"disambiguationData":[OSD([sQuery(id+"F0.wireOp",EDGE,"E0"),sQuery(id+"F0.wireOp",EDGE,"E6")])]});
            var Q1;
            Q1=makeQuery(id+"F1.opExtrude","SWEPT_EDGE",EDGE,{"disambiguationData":[OSD([sQuery(id+"F0.wireOp",EDGE,"E10"),sQuery(id+"F0.wireOp",EDGE,"E13.filletArc")])]});
            var Q2;
            Q2=makeQuery(id+"F1.opExtrude","SWEPT_EDGE",EDGE,{"disambiguationData":[OSD([sQuery(id+"F0.wireOp",EDGE,"E8"),sQuery(id+"F0.wireOp",EDGE,"E12.filletArc")])]});
            var Q3;
            Q3=makeQuery(id+"F1.opExtrude","SWEPT_EDGE",EDGE,{"disambiguationData":[OSD([sQuery(id+"F0.wireOp",EDGE,"E0"),sQuery(id+"F0.wireOp",EDGE,"E4")])]});
            var Q4;
            Q4=makeQuery(id+"F1.opExtrude","SWEPT_EDGE",EDGE,{"disambiguationData":[OSD([sQuery(id+"F0.wireOp",EDGE,"E0"),sQuery(id+"F0.wireOp",EDGE,"E15.1.5")])]});
            var Q5;
            Q5=makeQuery(id+"F1.opExtrude","SWEPT_EDGE",EDGE,{"disambiguationData":[OSD([sQuery(id+"F0.wireOp",EDGE,"E15.1.3"),sQuery(id+"F0.wireOp",EDGE,"E15.1.4")])]});
            var Q6;
            Q6=makeQuery(id+"F1.opExtrude","SWEPT_EDGE",EDGE,{"disambiguationData":[OSD([sQuery(id+"F0.wireOp",EDGE,"E15.1.1"),sQuery(id+"F0.wireOp",EDGE,"E15.1.2")])]});
            var Q7;
            Q7=makeQuery(id+"F1.opExtrude","SWEPT_EDGE",EDGE,{"disambiguationData":[OSD([sQuery(id+"F0.wireOp",EDGE,"E0"),sQuery(id+"F0.wireOp",EDGE,"E15.1.0")])]});
            var Q8;
            Q8=makeQuery(id+"F1.opExtrude","SWEPT_EDGE",EDGE,{"disambiguationData":[OSD([sQuery(id+"F0.wireOp",EDGE,"E0"),sQuery(id+"F0.wireOp",EDGE,"E15.2.5")])]});
            var Q9;
            Q9=makeQuery(id+"F1.opExtrude","SWEPT_EDGE",EDGE,{"disambiguationData":[OSD([sQuery(id+"F0.wireOp",EDGE,"E15.2.3"),sQuery(id+"F0.wireOp",EDGE,"E15.2.4")])]});
            var Q10;
            Q10=makeQuery(id+"F1.opExtrude","SWEPT_EDGE",EDGE,{"disambiguationData":[OSD([sQuery(id+"F0.wireOp",EDGE,"E0"),sQuery(id+"F0.wireOp",EDGE,"E15.2.0")])]});
            var Q11;
            Q11=makeQuery(id+"F1.opExtrude","SWEPT_EDGE",EDGE,{"disambiguationData":[OSD([sQuery(id+"F0.wireOp",EDGE,"E15.2.1"),sQuery(id+"F0.wireOp",EDGE,"E15.2.2")])]});
            var Q12;
            Q12=makeQuery(id+"F1.opExtrude","SWEPT_EDGE",EDGE,{"disambiguationData":[OSD([sQuery(id+"F0.wireOp",EDGE,"E0"),sQuery(id+"F0.wireOp",EDGE,"E15.3.5")])]});
            var Q13;
            Q13=makeQuery(id+"F1.opExtrude","SWEPT_EDGE",EDGE,{"disambiguationData":[OSD([sQuery(id+"F0.wireOp",EDGE,"E15.3.3"),sQuery(id+"F0.wireOp",EDGE,"E15.3.4")])]});
            var Q14;
            Q14=makeQuery(id+"F1.opExtrude","SWEPT_EDGE",EDGE,{"disambiguationData":[OSD([sQuery(id+"F0.wireOp",EDGE,"E15.3.1"),sQuery(id+"F0.wireOp",EDGE,"E15.3.2")])]});
            var Q15;
            {var subQ0=sQuery(id+"F0.wireOp",EDGE,"E15.3.0");var subQ1=sQuery(id+"F0.wireOp",EDGE,"E0");Q15=makeQuery(id+"F7.boolean.opBoolean","MERGE",EDGE,{"derivedFrom":[makeQuery(id+"F1.opExtrude","SWEPT_EDGE",EDGE,{"disambiguationData":[OSD([subQ1,subQ0])]}),makeQuery(id+"F7.opExtrude","SWEPT_EDGE",EDGE,{"disambiguationData":[OSD([subQ1,subQ0,sQuery(id+"F6.wireOp",EDGE,"E37")])]})]});}
            var Q16;
            Q16=makeQuery(id+"F1.opExtrude","SWEPT_EDGE",EDGE,{"disambiguationData":[OSD([sQuery(id+"F0.wireOp",EDGE,"E0"),sQuery(id+"F0.wireOp",EDGE,"E15.4.0")])]});
            var Q17;
            Q17=makeQuery(id+"F1.opExtrude","SWEPT_EDGE",EDGE,{"disambiguationData":[OSD([sQuery(id+"F0.wireOp",EDGE,"E15.4.1"),sQuery(id+"F0.wireOp",EDGE,"E15.4.2")])]});
            var Q18;
            Q18=makeQuery(id+"F1.opExtrude","SWEPT_EDGE",EDGE,{"disambiguationData":[OSD([sQuery(id+"F0.wireOp",EDGE,"E15.4.3"),sQuery(id+"F0.wireOp",EDGE,"E15.4.4")])]});
            var Q19;
            {var subQ0=sQuery(id+"F0.wireOp",EDGE,"E15.4.5");var subQ1=sQuery(id+"F0.wireOp",EDGE,"E0");Q19=makeQuery(id+"F7.boolean.opBoolean","MERGE",EDGE,{"derivedFrom":[makeQuery(id+"F1.opExtrude","SWEPT_EDGE",EDGE,{"disambiguationData":[OSD([subQ1,subQ0])]}),makeQuery(id+"F7.opExtrude","SWEPT_EDGE",EDGE,{"disambiguationData":[OSD([subQ1,subQ0,sQuery(id+"F6.wireOp",EDGE,"E38")])]})]});}
            var Q20;
            Q20=makeQuery(id+"F1.opExtrude","SWEPT_EDGE",EDGE,{"disambiguationData":[OSD([sQuery(id+"F0.wireOp",EDGE,"E0"),sQuery(id+"F0.wireOp",EDGE,"E15.5.5")])]});
            var Q21;
            Q21=makeQuery(id+"F1.opExtrude","SWEPT_EDGE",EDGE,{"disambiguationData":[OSD([sQuery(id+"F0.wireOp",EDGE,"E15.5.3"),sQuery(id+"F0.wireOp",EDGE,"E15.5.4")])]});
            var Q22;
            Q22=makeQuery(id+"F1.opExtrude","SWEPT_EDGE",EDGE,{"disambiguationData":[OSD([sQuery(id+"F0.wireOp",EDGE,"E15.5.1"),sQuery(id+"F0.wireOp",EDGE,"E15.5.2")])]});
            var Q23;
            {var subQ0=sQuery(id+"F0.wireOp",EDGE,"E15.5.0");var subQ1=sQuery(id+"F0.wireOp",EDGE,"E0");Q23=makeQuery(id+"F7.boolean.opBoolean","MERGE",EDGE,{"derivedFrom":[makeQuery(id+"F1.opExtrude","SWEPT_EDGE",EDGE,{"disambiguationData":[OSD([subQ1,subQ0])]}),makeQuery(id+"F7.opExtrude","SWEPT_EDGE",EDGE,{"disambiguationData":[OSD([subQ1,subQ0,sQuery(id+"F6.wireOp",EDGE,"E39")])]})]});}
            var Q24;
            {var subQ0=sQuery(id+"F0.wireOp",EDGE,"E15.6.5");var subQ1=sQuery(id+"F0.wireOp",EDGE,"E0");Q24=makeQuery(id+"F7.boolean.opBoolean","MERGE",EDGE,{"derivedFrom":[makeQuery(id+"F1.opExtrude","SWEPT_EDGE",EDGE,{"disambiguationData":[OSD([subQ1,subQ0])]}),makeQuery(id+"F7.opExtrude","SWEPT_EDGE",EDGE,{"disambiguationData":[OSD([subQ1,subQ0,sQuery(id+"F6.wireOp",EDGE,"E40")])]})]});}
            var Q25;
            Q25=makeQuery(id+"F1.opExtrude","SWEPT_EDGE",EDGE,{"disambiguationData":[OSD([sQuery(id+"F0.wireOp",EDGE,"E15.6.3"),sQuery(id+"F0.wireOp",EDGE,"E15.6.4")])]});
            var Q26;
            Q26=makeQuery(id+"F1.opExtrude","SWEPT_EDGE",EDGE,{"disambiguationData":[OSD([sQuery(id+"F0.wireOp",EDGE,"E15.6.1"),sQuery(id+"F0.wireOp",EDGE,"E15.6.2")])]});
            var Q27;
            Q27=makeQuery(id+"F1.opExtrude","SWEPT_EDGE",EDGE,{"disambiguationData":[OSD([sQuery(id+"F0.wireOp",EDGE,"E0"),sQuery(id+"F0.wireOp",EDGE,"E15.6.0")])]});
            var Q28;
            Q28=makeQuery(id+"F1.opExtrude","SWEPT_EDGE",EDGE,{"disambiguationData":[OSD([sQuery(id+"F0.wireOp",EDGE,"E0"),sQuery(id+"F0.wireOp",EDGE,"E15.7.5")])]});
            var Q29;
            Q29=makeQuery(id+"F1.opExtrude","SWEPT_EDGE",EDGE,{"disambiguationData":[OSD([sQuery(id+"F0.wireOp",EDGE,"E15.7.3"),sQuery(id+"F0.wireOp",EDGE,"E15.7.4")])]});
            var Q30;
            Q30=makeQuery(id+"F1.opExtrude","SWEPT_EDGE",EDGE,{"disambiguationData":[OSD([sQuery(id+"F0.wireOp",EDGE,"E15.7.1"),sQuery(id+"F0.wireOp",EDGE,"E15.7.2")])]});
            var Q31;
            Q31=makeQuery(id+"F1.opExtrude","SWEPT_EDGE",EDGE,{"disambiguationData":[OSD([sQuery(id+"F0.wireOp",EDGE,"E0"),sQuery(id+"F0.wireOp",EDGE,"E15.7.0")])]});
            var Q32;
            Q32=makeQuery(id+"F1.opExtrude","SWEPT_EDGE",EDGE,{"disambiguationData":[OSD([sQuery(id+"F0.wireOp",EDGE,"E0"),sQuery(id+"F0.wireOp",EDGE,"E15.8.5")])]});
            var Q33;
            Q33=makeQuery(id+"F1.opExtrude","SWEPT_EDGE",EDGE,{"disambiguationData":[OSD([sQuery(id+"F0.wireOp",EDGE,"E15.8.3"),sQuery(id+"F0.wireOp",EDGE,"E15.8.4")])]});
            var Q34;
            Q34=makeQuery(id+"F1.opExtrude","SWEPT_EDGE",EDGE,{"disambiguationData":[OSD([sQuery(id+"F0.wireOp",EDGE,"E15.8.1"),sQuery(id+"F0.wireOp",EDGE,"E15.8.2")])]});
            var Q35;
            Q35=makeQuery(id+"F1.opExtrude","SWEPT_EDGE",EDGE,{"disambiguationData":[OSD([sQuery(id+"F0.wireOp",EDGE,"E0"),sQuery(id+"F0.wireOp",EDGE,"E15.8.0")])]});
            fillet(context, id + "F8", {"entities" : qUnion([Q0, Q1, Q2, Q3, Q4, Q5, Q6, Q7, Q8, Q9, Q10, Q11, Q12, Q13, Q14, Q15, Q16, Q17, Q18, Q19, Q20, Q21, Q22, Q23, Q24, Q25, Q26, Q27, Q28, Q29, Q30, Q31, Q32, Q33, Q34, Q35]), "radius" : 0.76 * mm, "tangentPropagation" : true, "allowEdgeOverflow" : false});
        }
    });
